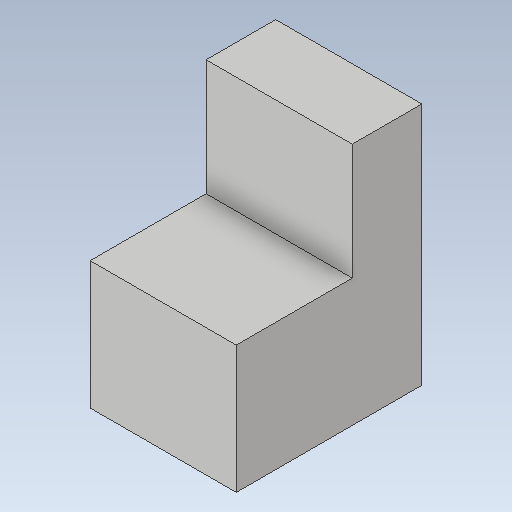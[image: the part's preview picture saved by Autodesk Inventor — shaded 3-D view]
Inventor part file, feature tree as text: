
AUTODESK INVENTOR PART (.ipt)
format: ipt  version: 2020 (Build 240168000, 168)  size: 137,728 bytes
history: native  units: mm
features: extrude x7, sketch x7
ambient origin geometry x8: Origin, YZ Plane, XZ Plane, XY Plane, X Axis, Y Axis, Z Axis, Center Point
bodies: Body1 (feature_tree)
feature tree (14):
  extrude  "Extrusion2"  Depth=220.0mm
  extrude  "Extrusion3"  Depth=120.0mm
  extrude  "Extrusion4"  Depth=200.0mm TaperAngle=0.0deg
  extrude  "Extrusion5"  Depth=72.0mm TaperAngle=0.0deg
  extrude  "Extrusion6"  Depth=20.0mm TaperAngle=0.0deg
  extrude  "Extrusion7"  [1 undecoded]
  extrude  "Extrusion8"  [1 undecoded]
  sketch  "Sketch2"  dims[d4=220.0mm d5=180.0mm]
  sketch  "Sketch3"  dims[d6=320.0mm d7=0.0mm d8=120.0mm]
  sketch  "Sketch4"  dims[d9=200.0mm d10=0.0mm d11=20.0mm d12=0.0mm]
  sketch  "Sketch5"  dims[d13=40.0mm d14=0.0mm d15=72.0mm d16=0.0mm]
  sketch  "Sketch6"  dims[d17=40.0mm d18=0.0mm d19=20.0mm d20=0.0mm]
  sketch  "Sketch7"
  sketch  "Sketch8"
note: 2 required parameter values undecoded (feature->parameter linkage not recoverable at this tier; creation-order binding heuristic only, values carry confidence <= 0.55)
